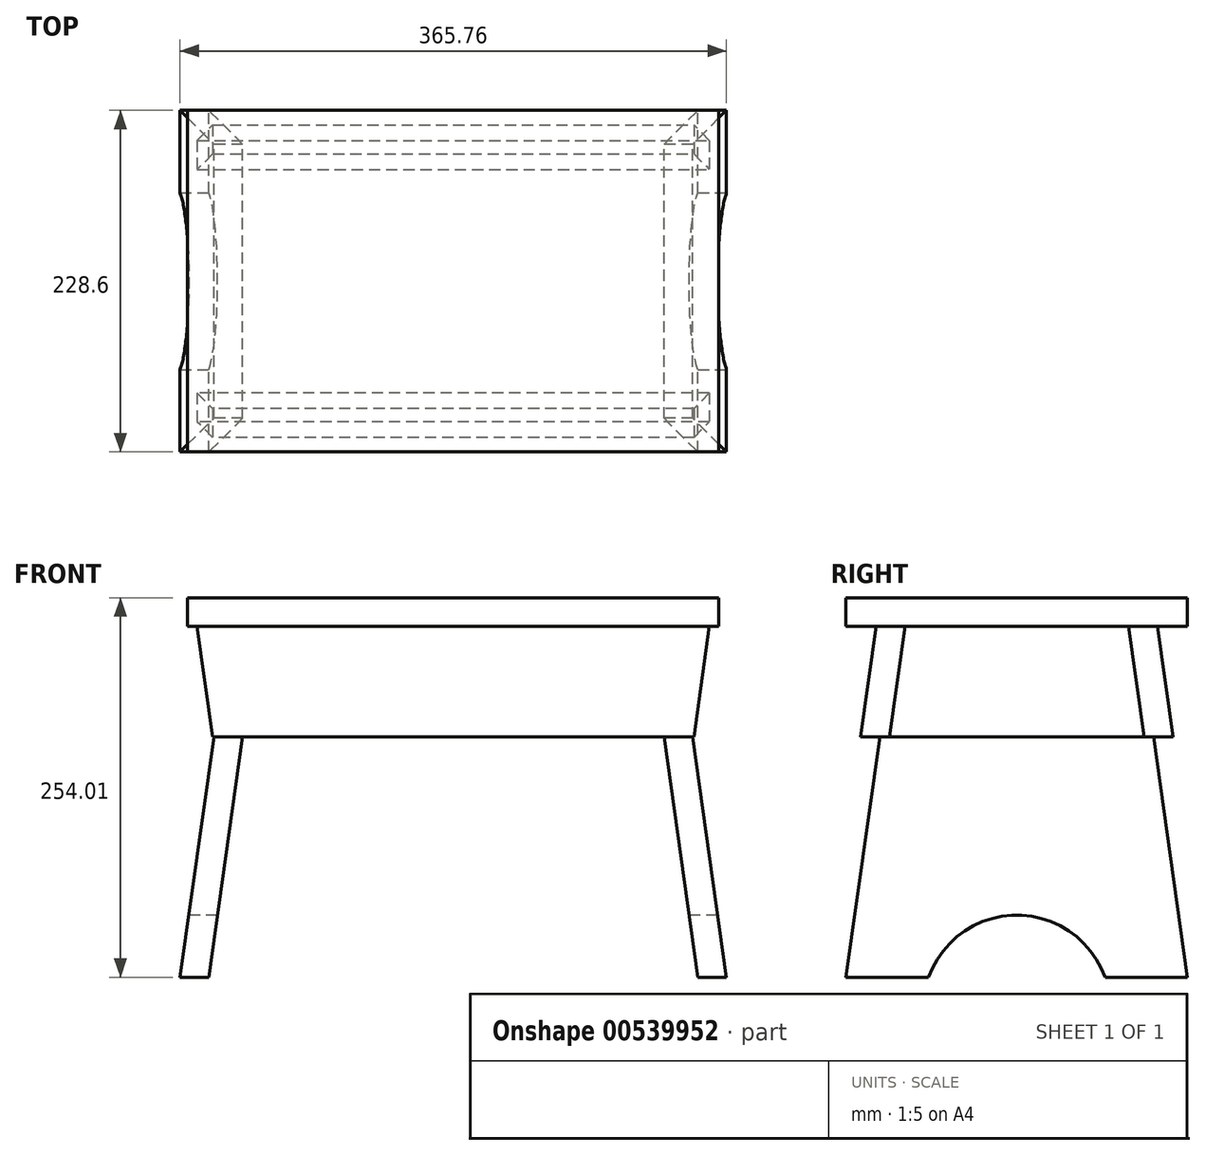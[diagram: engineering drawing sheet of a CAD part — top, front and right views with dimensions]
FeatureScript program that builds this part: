
annotation { "Feature Type Name" : "Feature", "Feature Type Description" : "" }
export const myFeature = defineFeature(function(context is Context, id is Id, definition is map)
    precondition{}
    {
        {
            var Q0;
            Q0=qCreatedBy(makeId("Front.planeOp"),FACE);
            var sketch = newSketch(context, id + "F0", { "sketchPlane" : qUnion([Q0])});
            skLineSegment(sketch, "E0.bottom", {"start": v(-177.8, 9.53) * mm, "end": v(177.8, 9.53) * mm});
            skLineSegment(sketch, "E0.top", {"start": v(-177.8, -9.53) * mm, "end": v(177.8, -9.53) * mm});
            skLineSegment(sketch, "E0.left", {"start": v(-177.8, 9.53) * mm, "end": v(-177.8, -9.52) * mm});
            skLineSegment(sketch, "E0.right", {"start": v(177.8, 9.53) * mm, "end": v(177.8, -9.52) * mm});
            skPoint(sketch, "E0.middle", {"position": v(0, 0) * mm});
            skLineSegment(sketch, "E1.bottom", {"start": v(-177.8, -9.53) * mm, "end": v(177.8, -9.53) * mm, "construction": true});
            skLineSegment(sketch, "E1.top", {"start": v(-177.8, -244.47) * mm, "end": v(177.8, -244.47) * mm, "construction": true});
            skLineSegment(sketch, "E1.left", {"start": v(-177.8, -9.52) * mm, "end": v(-177.8, -244.47) * mm, "construction": true});
            skLineSegment(sketch, "E1.right", {"start": v(177.8, -9.52) * mm, "end": v(177.8, -244.47) * mm, "construction": true});
            skLineSegment(sketch, "E2", {"start": v(0, 0) * mm, "end": v(0, -244.47) * mm, "construction": true});
            skLineSegment(sketch, "E3.MirrorCS", {"start": v(-149.47, -244.47) * mm, "end": v(-130.03, -244.47) * mm});
            skLineSegment(sketch, "E4.top", {"start": v(-177.8, -83.71) * mm, "end": v(177.8, -83.71) * mm});
            skLineSegment(sketch, "E4.left", {"start": v(-177.8, -9.52) * mm, "end": v(-177.8, -83.71) * mm});
            skLineSegment(sketch, "E4.right", {"start": v(177.8, -9.52) * mm, "end": v(177.8, -83.71) * mm});
            skLineSegment(sketch, "E5", {"start": v(171.45, -9.52) * mm, "end": v(161.02, -83.71) * mm});
            skLineSegment(sketch, "E6.MirrorCS", {"start": v(-171.45, -9.52) * mm, "end": v(-161.02, -83.71) * mm});
            skLineSegment(sketch, "E7", {"start": v(149.86, -9.52) * mm, "end": v(182.88, -244.47) * mm});
            skLineSegment(sketch, "E8", {"start": v(182.88, -244.47) * mm, "end": v(163.64, -244.47) * mm});
            skLineSegment(sketch, "E9", {"start": v(163.64, -244.47) * mm, "end": v(130.62, -9.52) * mm});
            skLineSegment(sketch, "E10", {"start": v(130.62, -9.53) * mm, "end": v(149.86, -9.53) * mm});
            skLineSegment(sketch, "E11.MirrorCS", {"start": v(-149.86, -9.52) * mm, "end": v(-182.88, -244.47) * mm});
            skLineSegment(sketch, "E12.MirrorCS", {"start": v(-163.64, -244.47) * mm, "end": v(-130.62, -9.53) * mm});
            skLineSegment(sketch, "E13.MirrorCS", {"start": v(-182.88, -244.47) * mm, "end": v(-163.64, -244.47) * mm});
            skLineSegment(sketch, "E14.MirrorCS", {"start": v(-130.62, -9.53) * mm, "end": v(-149.86, -9.53) * mm});
            skSolve(sketch);
        }
        {
            var Q0;
            Q0=makeQuery(id+"F0.imprint","IMPRINT",FACE,{"disambiguationData":[TD([[makeQuery(id+"F0.imprint","IMPRINT",EDGE,{"derivedFrom":sQuery(id+"F0.wireOp",EDGE,"E0.bottom")}),-1.0]])]});
            extrude(context, id + "F1", {"entities" : qUnion([Q0]), "endBound" : BoundingType.SYMMETRIC, "depth" : 228.6 * mm, "offsetDistance" : 25.4 * mm});
        }
        {
            var Q0;
            {var subQ0=sQuery(id+"F0.wireOp",EDGE,"E13.MirrorCS");Q0=makeQuery(id+"F0.imprint","IMPRINT",FACE,{"disambiguationData":[TD([[makeQuery(id+"F0.imprint","IMPRINT",EDGE,{"derivedFrom":subQ0}),1.0]])]});}
            var Q1;
            {var subQ0=sQuery(id+"F0.wireOp",EDGE,"E14.MirrorCS");Q1=makeQuery(id+"F0.imprint","IMPRINT",FACE,{"disambiguationData":[TD([[makeQuery(id+"F0.imprint","IMPRINT",EDGE,{"derivedFrom":subQ0}),1.0]])]});}
            var Q2;
            {var subQ0=sQuery(id+"F0.wireOp",EDGE,"E8");Q2=makeQuery(id+"F0.imprint","IMPRINT",FACE,{"disambiguationData":[TD([[makeQuery(id+"F0.imprint","IMPRINT",EDGE,{"derivedFrom":subQ0}),-1.0]])]});}
            var Q3;
            {var subQ0=sQuery(id+"F0.wireOp",EDGE,"E10");Q3=makeQuery(id+"F0.imprint","IMPRINT",FACE,{"disambiguationData":[TD([[makeQuery(id+"F0.imprint","IMPRINT",EDGE,{"derivedFrom":subQ0}),-1.0]])]});}
            var Q4;
            Q4=makeQuery(id+"F1.opExtrude","CAP_VERTEX",VERTEX,{"disambiguationData":[OSD([sQuery(id+"F0.wireOp",EDGE,"E0.right"),sQuery(id+"F0.wireOp",EDGE,"E0.top"),sQuery(id+"F0.wireOp",EDGE,"E4.right")])],"isStart":false});
            var Q5;
            Q5=makeQuery(id+"F1.opExtrude","CAP_VERTEX",VERTEX,{"disambiguationData":[OSD([sQuery(id+"F0.wireOp",EDGE,"E0.right"),sQuery(id+"F0.wireOp",EDGE,"E0.top"),sQuery(id+"F0.wireOp",EDGE,"E4.right")])],"isStart":true});
            extrude(context, id + "F2", {"entities" : qUnion([Q0, Q1, Q2, Q3]), "endBound" : BoundingType.UP_TO_VERTEX, "depth" : 42.93 * mm, "endBoundEntityVertex" : qUnion([Q4]), "offsetDistance" : 25.4 * mm, "hasSecondDirection" : true, "secondDirectionBound" : SecondDirectionBoundingType.UP_TO_VERTEX, "secondDirectionOppositeDirection" : true, "secondDirectionDepth" : 25.4 * mm, "secondDirectionBoundEntityVertex" : qUnion([Q5])});
        }
        {
            var Q0;
            Q0=qCreatedBy(makeId("Right.planeOp"),FACE);
            var sketch = newSketch(context, id + "F3", { "sketchPlane" : qUnion([Q0])});
            skLineSegment(sketch, "E15.0.0", {"start": v(114.3, -9.53) * mm, "end": v(-114.3, -9.53) * mm});
            skLineSegment(sketch, "E15.0.1", {"start": v(-114.3, -9.53) * mm, "end": v(-114.3, -244.47) * mm});
            skLineSegment(sketch, "E15.0.2", {"start": v(-114.3, -244.47) * mm, "end": v(114.3, -244.47) * mm});
            skLineSegment(sketch, "E15.0.3", {"start": v(114.3, -244.47) * mm, "end": v(114.3, -9.53) * mm});
            skLineSegment(sketch, "E16", {"start": v(-114.3, -244.48) * mm, "end": v(-81.28, -9.52) * mm});
            skLineSegment(sketch, "E17.MirrorCS", {"start": v(114.3, -244.47) * mm, "end": v(81.28, -9.52) * mm});
            skArc(sketch, "E18", {"start": v(59.07, -244.47) * mm, "mid": v(0, -202.82) * mm, "end": v(-59.07, -244.47) * mm});
            skLineSegment(sketch, "E19", {"start": v(0, -265.53) * mm, "end": v(0, -244.47) * mm, "construction": true});
            skSolve(sketch);
        }
        {
            var Q0;
            {var subQ0=sQuery(id+"F3.wireOp",EDGE,"E15.0.1");Q0=makeQuery(id+"F3.imprint","IMPRINT",FACE,{"disambiguationData":[TD([[makeQuery(id+"F3.imprint","IMPRINT",EDGE,{"derivedFrom":subQ0}),1.0]])]});}
            var Q1;
            {var subQ0=sQuery(id+"F3.wireOp",EDGE,"E18");Q1=makeQuery(id+"F3.imprint","IMPRINT",FACE,{"disambiguationData":[TD([[makeQuery(id+"F3.imprint","IMPRINT",EDGE,{"derivedFrom":subQ0}),1.0]])]});}
            var Q2;
            {var subQ0=sQuery(id+"F3.wireOp",EDGE,"E15.0.3");Q2=makeQuery(id+"F3.imprint","IMPRINT",FACE,{"disambiguationData":[TD([[makeQuery(id+"F3.imprint","IMPRINT",EDGE,{"derivedFrom":subQ0}),1.0]])]});}
            extrude(context, id + "F4", {"entities" : qUnion([Q0, Q1, Q2]), "operationType" : NewBodyOperationType.REMOVE, "endBound" : BoundingType.THROUGH_ALL, "oppositeDirection" : true, "depth" : 25.4 * mm, "offsetDistance" : 25.4 * mm, "hasSecondDirection" : true, "secondDirectionBound" : SecondDirectionBoundingType.THROUGH_ALL, "secondDirectionOppositeDirection" : false, "secondDirectionDepth" : 25.4 * mm});
        }
        {
            var Q0;
            Q0=qCreatedBy(makeId("Right.planeOp"),FACE);
            var sketch = newSketch(context, id + "F5", { "sketchPlane" : qUnion([Q0])});
            skLineSegment(sketch, "E20.0", {"start": v(-81.28, -9.53) * mm, "end": v(-114.3, -244.48) * mm});
            skLineSegment(sketch, "E21.0", {"start": v(-114.3, -9.52) * mm, "end": v(114.3, -9.52) * mm});
            skLineSegment(sketch, "E22", {"start": v(-94.1, -9.52) * mm, "end": v(-104.53, -83.71) * mm});
            skLineSegment(sketch, "E23", {"start": v(-104.53, -83.71) * mm, "end": v(-85.3, -83.71) * mm});
            skLineSegment(sketch, "E24", {"start": v(-85.3, -83.71) * mm, "end": v(-74.87, -9.52) * mm});
            skLineSegment(sketch, "E25", {"start": v(-74.87, -9.52) * mm, "end": v(-94.1, -9.52) * mm});
            skLineSegment(sketch, "E26", {"start": v(-85.3, -83.71) * mm, "end": v(85.3, -83.71) * mm, "construction": true});
            skLineSegment(sketch, "E27.MirrorCS", {"start": v(74.87, -9.52) * mm, "end": v(94.1, -9.52) * mm});
            skLineSegment(sketch, "E28.MirrorCS", {"start": v(104.53, -83.71) * mm, "end": v(85.3, -83.71) * mm});
            skLineSegment(sketch, "E29.MirrorCS", {"start": v(81.28, -9.53) * mm, "end": v(114.3, -244.48) * mm});
            skLineSegment(sketch, "E30.MirrorCS", {"start": v(94.1, -9.52) * mm, "end": v(104.53, -83.71) * mm});
            skLineSegment(sketch, "E31.MirrorCS", {"start": v(85.3, -83.71) * mm, "end": v(74.87, -9.52) * mm});
            skSolve(sketch);
        }
        {
            var Q0;
            {var subQ5=sQuery(id+"F5.wireOp",EDGE,"E22");Q0=makeQuery(id+"F5.imprint","IMPRINT",FACE,{"disambiguationData":[TD([[makeQuery(id+"F5.imprint","IMPRINT",EDGE,{"derivedFrom":subQ5}),1.0]])]});}
            var Q1;
            {var subQ5=sQuery(id+"F5.wireOp",EDGE,"E24");Q1=makeQuery(id+"F5.imprint","IMPRINT",FACE,{"disambiguationData":[TD([[makeQuery(id+"F5.imprint","IMPRINT",EDGE,{"derivedFrom":subQ5}),1.0]])]});}
            var Q2;
            {var subQ5=sQuery(id+"F5.wireOp",EDGE,"2da5aad2-97e1-4465-ba79-64436e5bf7d11.MirrorCS");Q2=makeQuery(id+"F5.imprint","IMPRINT",FACE,{"disambiguationData":[TD([[makeQuery(id+"F5.imprint","IMPRINT",EDGE,{"derivedFrom":subQ5}),-1.0]])]});}
            var Q3;
            {var subQ5=sQuery(id+"F5.wireOp",EDGE,"2da5aad2-97e1-4465-ba79-64436e5bf7d12.MirrorCS");Q3=makeQuery(id+"F5.imprint","IMPRINT",FACE,{"disambiguationData":[TD([[makeQuery(id+"F5.imprint","IMPRINT",EDGE,{"derivedFrom":subQ5}),-1.0]])]});}
            var Q4;
            Q4=makeQuery(id+"F1.opExtrude","SWEPT_FACE",FACE,{"disambiguationData":[OSD([sQuery(id+"F0.wireOp",EDGE,"E0.right")])]});
            var Q5;
            Q5=makeQuery(id+"F1.opExtrude","SWEPT_FACE",FACE,{"disambiguationData":[OSD([sQuery(id+"F0.wireOp",EDGE,"E0.left")])]});
            extrude(context, id + "F6", {"entities" : qUnion([Q0, Q1, Q2, Q3]), "endBound" : BoundingType.UP_TO_SURFACE, "depth" : 25.4 * mm, "endBoundEntityFace" : qUnion([Q4]), "offsetDistance" : 25.4 * mm, "hasSecondDirection" : true, "secondDirectionBound" : SecondDirectionBoundingType.UP_TO_SURFACE, "secondDirectionOppositeDirection" : true, "secondDirectionDepth" : 25.4 * mm, "secondDirectionBoundEntityFace" : qUnion([Q5])});
        }
        {
            var Q0;
            {var subQ5=sQuery(id+"F0.wireOp",EDGE,"E4.left");Q0=makeQuery(id+"F0.imprint","IMPRINT",FACE,{"disambiguationData":[TD([[makeQuery(id+"F0.imprint","IMPRINT",EDGE,{"derivedFrom":subQ5}),1.0]])]});}
            var Q1;
            {var subQ0=sQuery(id+"F0.wireOp",EDGE,"E4.right");Q1=makeQuery(id+"F0.imprint","IMPRINT",FACE,{"disambiguationData":[TD([[makeQuery(id+"F0.imprint","IMPRINT",EDGE,{"derivedFrom":subQ0}),-1.0]])]});}
            extrude(context, id + "F7", {"entities" : qUnion([Q0, Q1]), "operationType" : NewBodyOperationType.REMOVE, "endBound" : BoundingType.THROUGH_ALL, "oppositeDirection" : true, "depth" : 25.4 * mm, "offsetDistance" : 25.4 * mm, "hasSecondDirection" : true, "secondDirectionBound" : SecondDirectionBoundingType.THROUGH_ALL, "secondDirectionOppositeDirection" : false, "secondDirectionDepth" : 25.4 * mm});
        }
        {
            var Q0;
            {var subQ0=sQuery(id+"F5.wireOp",EDGE,"E30.MirrorCS");Q0=makeQuery(id+"F5.imprint","IMPRINT",FACE,{"disambiguationData":[TD([[makeQuery(id+"F5.imprint","IMPRINT",EDGE,{"derivedFrom":subQ0}),-1.0]])]});}
            var Q1;
            {var subQ0=sQuery(id+"F5.wireOp",EDGE,"E31.MirrorCS");Q1=makeQuery(id+"F5.imprint","IMPRINT",FACE,{"disambiguationData":[TD([[makeQuery(id+"F5.imprint","IMPRINT",EDGE,{"derivedFrom":subQ0}),-1.0]])]});}
            var Q2;
            Q2=makeQuery(id+"F1.opExtrude","SWEPT_FACE",FACE,{"disambiguationData":[OSD([sQuery(id+"F0.wireOp",EDGE,"E0.left")])]});
            var Q3;
            Q3=makeQuery(id+"F1.opExtrude","SWEPT_FACE",FACE,{"disambiguationData":[OSD([sQuery(id+"F0.wireOp",EDGE,"E0.right")])]});
            extrude(context, id + "F8", {"entities" : qUnion([Q0, Q1]), "endBound" : BoundingType.UP_TO_SURFACE, "oppositeDirection" : true, "depth" : 25.4 * mm, "endBoundEntityFace" : qUnion([Q2]), "offsetDistance" : 25.4 * mm, "hasSecondDirection" : true, "secondDirectionBound" : SecondDirectionBoundingType.UP_TO_SURFACE, "secondDirectionOppositeDirection" : false, "secondDirectionDepth" : 25.4 * mm, "secondDirectionBoundEntityFace" : qUnion([Q3])});
        }
        {
            var Q0;
            Q0=makeQuery(id+"F2.opExtrude","SWEPT_BODY",BODY,{"disambiguationData":[OSD([sQuery(id+"F0.wireOp",EDGE,"E11.MirrorCS"),sQuery(id+"F0.wireOp",EDGE,"E12.MirrorCS"),sQuery(id+"F0.wireOp",EDGE,"E13.MirrorCS"),sQuery(id+"F0.wireOp",EDGE,"E14.MirrorCS")])]});
            var Q1;
            Q1=makeQuery(id+"F8.opExtrude","SWEPT_BODY",BODY,{"disambiguationData":[OSD([sQuery(id+"F5.wireOp",EDGE,"E27.MirrorCS"),sQuery(id+"F5.wireOp",EDGE,"E28.MirrorCS"),sQuery(id+"F5.wireOp",EDGE,"E30.MirrorCS"),sQuery(id+"F5.wireOp",EDGE,"E31.MirrorCS")])]});
            booleanBodies(context, id + "F9", {"operationType" : BooleanOperationType.SUBTRACTION, "tools" : qUnion([Q0]), "targets" : qUnion([Q1]), "keepTools" : true});
        }
        {
            var Q0;
            Q0=makeQuery(id+"F2.opExtrude","SWEPT_BODY",BODY,{"disambiguationData":[OSD([sQuery(id+"F0.wireOp",EDGE,"E11.MirrorCS"),sQuery(id+"F0.wireOp",EDGE,"E12.MirrorCS"),sQuery(id+"F0.wireOp",EDGE,"E13.MirrorCS"),sQuery(id+"F0.wireOp",EDGE,"E14.MirrorCS")])]});
            var Q1;
            Q1=makeQuery(id+"F6.opExtrude","SWEPT_BODY",BODY,{"disambiguationData":[OSD([sQuery(id+"F5.wireOp",EDGE,"E22"),sQuery(id+"F5.wireOp",EDGE,"E23"),sQuery(id+"F5.wireOp",EDGE,"E24"),sQuery(id+"F5.wireOp",EDGE,"E25")])]});
            booleanBodies(context, id + "F10", {"operationType" : BooleanOperationType.SUBTRACTION, "tools" : qUnion([Q0]), "targets" : qUnion([Q1]), "keepTools" : true});
        }
        {
            var Q0;
            Q0=makeQuery(id+"F2.opExtrude","SWEPT_BODY",BODY,{"disambiguationData":[OSD([sQuery(id+"F0.wireOp",EDGE,"E7"),sQuery(id+"F0.wireOp",EDGE,"E8"),sQuery(id+"F0.wireOp",EDGE,"E9"),sQuery(id+"F0.wireOp",EDGE,"E10")])]});
            var Q1;
            Q1=makeQuery(id+"F6.opExtrude","SWEPT_BODY",BODY,{"disambiguationData":[OSD([sQuery(id+"F5.wireOp",EDGE,"E22"),sQuery(id+"F5.wireOp",EDGE,"E23"),sQuery(id+"F5.wireOp",EDGE,"E24"),sQuery(id+"F5.wireOp",EDGE,"E25")])]});
            booleanBodies(context, id + "F11", {"operationType" : BooleanOperationType.SUBTRACTION, "tools" : qUnion([Q0]), "targets" : qUnion([Q1]), "keepTools" : true});
        }
        {
            var Q0;
            Q0=makeQuery(id+"F2.opExtrude","SWEPT_BODY",BODY,{"disambiguationData":[OSD([sQuery(id+"F0.wireOp",EDGE,"E7"),sQuery(id+"F0.wireOp",EDGE,"E8"),sQuery(id+"F0.wireOp",EDGE,"E9"),sQuery(id+"F0.wireOp",EDGE,"E10")])]});
            var Q1;
            Q1=makeQuery(id+"F8.opExtrude","SWEPT_BODY",BODY,{"disambiguationData":[OSD([sQuery(id+"F5.wireOp",EDGE,"E27.MirrorCS"),sQuery(id+"F5.wireOp",EDGE,"E28.MirrorCS"),sQuery(id+"F5.wireOp",EDGE,"E30.MirrorCS"),sQuery(id+"F5.wireOp",EDGE,"E31.MirrorCS")])]});
            booleanBodies(context, id + "F12", {"operationType" : BooleanOperationType.SUBTRACTION, "tools" : qUnion([Q0]), "targets" : qUnion([Q1]), "keepTools" : true});
        }
        {
            var Q0;
            {var subQ0=sQuery(id+"F0.wireOp",EDGE,"E4.right");Q0=makeQuery(id+"F0.imprint","IMPRINT",FACE,{"disambiguationData":[TD([[makeQuery(id+"F0.imprint","IMPRINT",EDGE,{"derivedFrom":subQ0}),-1.0]])]});}
            extrude(context, id + "F13", {"entities" : qUnion([Q0]), "operationType" : NewBodyOperationType.REMOVE, "endBound" : BoundingType.THROUGH_ALL, "oppositeDirection" : true, "depth" : 25.4 * mm, "offsetDistance" : 25.4 * mm});
        }
        {
            var Q0;
            {var subQ0=sQuery(id+"F0.wireOp",EDGE,"E4.left");Q0=makeQuery(id+"F0.imprint","IMPRINT",FACE,{"disambiguationData":[TD([[makeQuery(id+"F0.imprint","IMPRINT",EDGE,{"derivedFrom":subQ0}),1.0]])]});}
            extrude(context, id + "F14", {"entities" : qUnion([Q0]), "operationType" : NewBodyOperationType.REMOVE, "endBound" : BoundingType.THROUGH_ALL, "oppositeDirection" : true, "depth" : 25.4 * mm, "offsetDistance" : 25.4 * mm});
        }
    });
